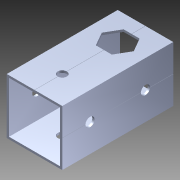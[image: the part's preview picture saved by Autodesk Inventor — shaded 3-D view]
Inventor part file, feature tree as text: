
AUTODESK INVENTOR PART (.ipt)
format: ipt  version: 2014 (Build 180170000, 170)  size: 1,181,696 bytes
history: native  units: in
note: dims shown in document units (in); Inventor stores cm internally (conversion verified against a paired STEP export)
features: extrude x2, sketch x2, pattern_circular x1, other x1, plane x1, imported_body x1
ambient origin geometry x8: Origin, YZ Plane, XZ Plane, XY Plane, X Axis, Y Axis, Z Axis, Center Point
bodies: Body1 (feature_tree)
feature tree (8):
  pattern_circular  "CirPattern2"
  other  "217-3426-STEP1"
  plane  "Work Plane1"
  extrude  "Extrusion1"  Depth=3937.0079in TaperAngle=0.0deg
  extrude  "Extrusion2"  Depth=2.0in TaperAngle=0.0deg
  imported_body  "Base1"
  sketch  "Sketch1"  dims[d0=-2.0in d1=3937.0079in d2=0.0in]
  sketch  "Sketch3"  dims[d3=0.5in d4=2.0in d5=0.0in]
